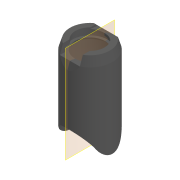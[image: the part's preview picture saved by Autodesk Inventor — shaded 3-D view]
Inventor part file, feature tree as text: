
AUTODESK INVENTOR PART (.ipt)
format: ipt  version: 2020 (Build 240168000, 168)  size: 290,304 bytes
history: native  units: mm
features: sketch x12, extrude x10, revolve x2, plane x2, projected_geometry x2
ambient origin geometry x8: Origin, YZ Plane, XZ Plane, XY Plane, X Axis, Y Axis, Z Axis, Center Point
bodies: Solid1 (feature_tree)
feature tree (28):
  revolve  "Revolution1"  [1 undecoded]
  extrude  "Extrusion1"  Depth=1.1184mm
  extrude  "Extrusion2"  Depth=12.5mm TaperAngle=0.0deg
  extrude  "Extrusion3"  Depth=1.5mm
  extrude  "Extrusion4"  Depth=1.2mm
  plane  "Work Plane1"
  extrude  "Extrusion5"  Depth=24.534mm
  revolve  "Revolution2"  [1 undecoded]
  extrude  "Extrusion6"  Depth=3.99mm
  extrude  "Extrusion7"  Depth=4.6mm
  extrude  "Extrusion8"  Depth=12.5mm TaperAngle=0.0deg
  extrude  "Extrusion9"  Depth=1.239184mm
  plane  "Work Plane2"
  extrude  "Extrusion11"  Depth=18.5mm
  sketch  "Sketch1"  dims[d0=10.33mm d10=2.3mm]
  sketch  "Sketch2"  dims[d11=1.2mm d12=1.1184mm]
  sketch  "Sketch3"  dims[d15=90.0deg d18=12.5mm d19=0.0mm]
  sketch  "Sketch4"  dims[d20=1.5mm d21=1.93mm]
  sketch  "Sketch5"  dims[d22=2.5mm d23=1.2mm]
  sketch  "Sketch6"  dims[d24=4.0mm d25=24.534mm]
  projected_geometry  "Projected Loop1"
  sketch  "Sketch7"  dims[d26=1.45mm d27=0.3547mm]
  sketch  "Sketch8"  dims[d28=4.6mm d29=3.99mm]
  sketch  "Sketch9"  dims[d30=12.5mm d31=0.0mm d32=4.6mm]
  sketch  "Sketch10"  dims[d33=0.62mm d34=12.5mm d35=0.0mm]
  sketch  "Sketch11"  dims[d36=0.01mm d37=0.0mm d38=1.239184mm]
  sketch  "Sketch13"  dims[d39=1.51mm d40=0.551mm d41=0.0mm d42=0.0mm d43=0.808mm d44=1.4269mm d45=90.0deg d46=10.0mm d47=46.75mm d48=0.0mm d49=46.75mm d50=0.0mm d51=2.4mm d52=10.0mm d53=10.125mm d54=0.0mm d55=0.0mm d56=15.5mm d57=0.0mm d61=6.0mm d62=18.5mm d63=0.0mm]
  projected_geometry  "Projected Loop2"
note: 2 required parameter values undecoded (feature->parameter linkage not recoverable at this tier; creation-order binding heuristic only, values carry confidence <= 0.55)
